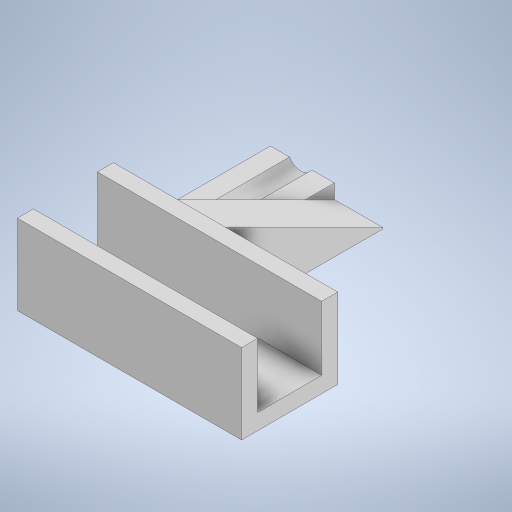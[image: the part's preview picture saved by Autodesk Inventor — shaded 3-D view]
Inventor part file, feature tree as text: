
AUTODESK INVENTOR PART (.ipt)
format: ipt  version: 2024 (Build 280153000, 153)  size: 267,776 bytes
history: native  units: mm
features: extrude x6, sketch x6
ambient origin geometry x8: Origin, YZ Plane, XZ Plane, XY Plane, X Axis, Y Axis, Z Axis, Center Point
bodies: Solid1 (feature_tree)
feature tree (12):
  extrude  "Extrusion1"  Depth=70.0mm
  extrude  "Extrusion2"  Depth=30.0mm
  extrude  "Extrusion3"  Depth=50.0mm
  extrude  "Extrusion4"  Depth=40.0mm
  extrude  "Extrusion5"  Depth=140.0mm TaperAngle=0.0deg
  extrude  "Extrusion6"  Depth=30.0mm TaperAngle=0.0deg
  sketch  "Sketch1"  dims[d0=100.0mm d1=70.0mm]
  sketch  "Sketch2"  dims[d2=30.0mm d3=80.0mm]
  sketch  "Sketch4"  dims[d4=10.0mm d5=0.0mm d6=50.0mm]
  sketch  "Sketch6"  dims[d7=50.0mm d8=40.0mm]
  sketch  "Sketch7"  dims[d9=40.0mm d10=140.0mm d11=0.0mm]
  sketch  "Sketch8"  dims[d12=50.0mm d13=0.0mm d14=30.0mm d15=0.0mm d16=1000.0mm d17=0.0mm d18=10.0mm d19=1000.0mm d20=0.0mm]
